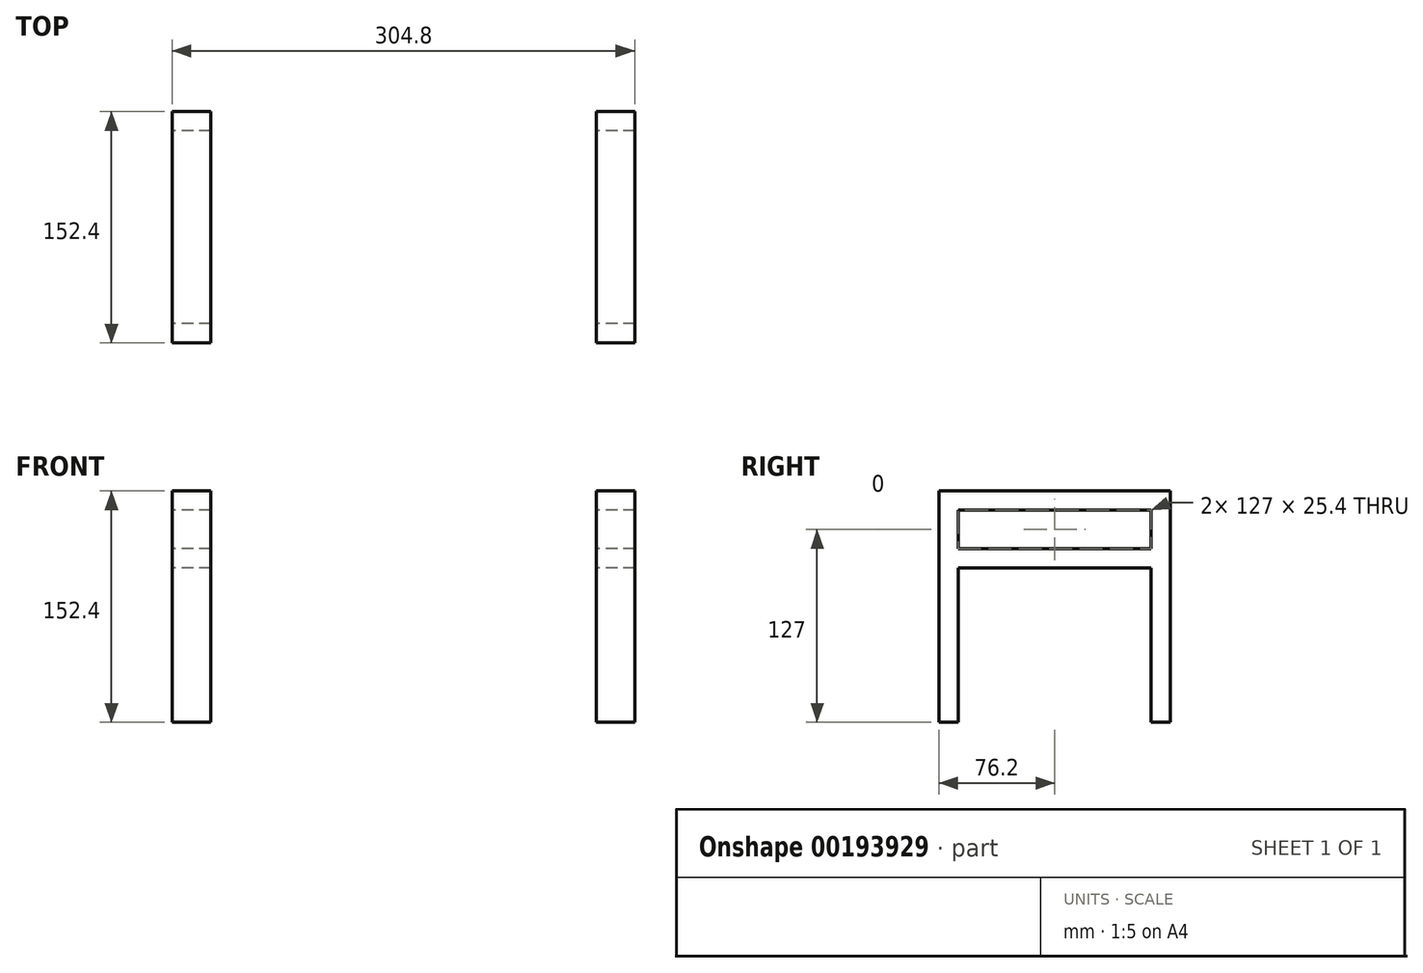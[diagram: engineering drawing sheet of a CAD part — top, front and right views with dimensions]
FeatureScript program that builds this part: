
annotation { "Feature Type Name" : "Feature", "Feature Type Description" : "" }
export const myFeature = defineFeature(function(context is Context, id is Id, definition is map)
    precondition{}
    {
        {
            var Q0;
            Q0=qCreatedBy(makeId("Front.planeOp"),FACE);
            var sketch = newSketch(context, id + "F0", { "sketchPlane" : qUnion([Q0])});
            skLineSegment(sketch, "E0.bottom", {"start": v(-150.3, 73.22) * mm, "end": v(154.5, 73.22) * mm});
            skLineSegment(sketch, "E0.top", {"start": v(-150.3, -79.18) * mm, "end": v(154.5, -79.18) * mm});
            skLineSegment(sketch, "E0.left", {"start": v(-150.3, 73.22) * mm, "end": v(-150.3, -79.18) * mm});
            skLineSegment(sketch, "E0.right", {"start": v(154.5, 73.22) * mm, "end": v(154.5, -79.18) * mm});
            skSolve(sketch);
        }
        {
            var Q0;
            Q0 = qSketchRegion(id + "F0", true);
            extrude(context, id + "F1", {"entities" : qUnion([Q0]), "depth" : 152.4 * mm});
        }
        {
            var Q0;
            Q0=makeQuery(id+"F1.opExtrude","SWEPT_FACE",FACE,{"disambiguationData":[OSD([sQuery(id+"F0.wireOp",EDGE,"E0.left")])]});
            var sketch = newSketch(context, id + "F2", { "sketchPlane" : qUnion([Q0])});
            skLineSegment(sketch, "E1.0", {"start": v(152.4, 60.52) * mm, "end": v(0, 60.52) * mm});
            skLineSegment(sketch, "E2.0", {"start": v(12.7, 73.22) * mm, "end": v(12.7, -79.18) * mm});
            skLineSegment(sketch, "E3.0", {"start": v(139.7, 73.22) * mm, "end": v(139.7, -79.18) * mm});
            skLineSegment(sketch, "E4.0", {"start": v(152.4, 35.12) * mm, "end": v(0, 35.12) * mm});
            skLineSegment(sketch, "E5.0", {"start": v(152.4, 22.42) * mm, "end": v(0, 22.42) * mm});
            skSolve(sketch);
        }
        {
            var Q0;
            {var subQ0=sQuery(id+"F2.wireOp",EDGE,"E3.0");var subQ1=sQuery(id+"F2.wireOp",EDGE,"E1.0");var subQ2=makeQuery(id+"F2.imprint","INTERSECT",VERTEX,{"derivedFrom":[subQ1,subQ0]});Q0=makeQuery(id+"F2.imprint","IMPRINT",FACE,{"disambiguationData":[TD([[makeQuery(id+"F2.imprint","IMPRINT",EDGE,{"disambiguationData":[TD([[subQ2,-1.0]])],"derivedFrom":subQ1}),1.0]])]});}
            var Q1;
            {var subQ0=sQuery(id+"F2.wireOp",EDGE,"E2.0");var subQ3=sQuery(id+"F2.wireOp",EDGE,"E5.0");var subQ4=makeQuery(id+"F2.imprint","INTERSECT",VERTEX,{"derivedFrom":[subQ0,subQ3]});Q1=makeQuery(id+"F2.imprint","IMPRINT",FACE,{"disambiguationData":[TD([[makeQuery(id+"F2.imprint","IMPRINT",EDGE,{"disambiguationData":[TD([[subQ4,1.0]])],"derivedFrom":subQ3}),1.0]])]});}
            extrude(context, id + "F3", {"entities" : qUnion([Q0, Q1]), "operationType" : NewBodyOperationType.REMOVE, "oppositeDirection" : true, "depth" : 304.8 * mm});
        }
        {
            var Q0;
            Q0=makeQuery(id+"F1.opExtrude","SWEPT_FACE",FACE,{"disambiguationData":[OSD([sQuery(id+"F0.wireOp",EDGE,"E0.bottom")])]});
            var sketch = newSketch(context, id + "F4", { "sketchPlane" : qUnion([Q0])});
            skLineSegment(sketch, "E6.0", {"start": v(-124.9, -152.4) * mm, "end": v(-124.9, 0) * mm});
            skLineSegment(sketch, "E7.0", {"start": v(129.1, -152.4) * mm, "end": v(129.1, 0) * mm});
            skSolve(sketch);
        }
        {
            var Q0;
            {var subQ0=sQuery(id+"F4.wireOp",EDGE,"E6.0");Q0=makeQuery(id+"F4.imprint","IMPRINT",FACE,{"disambiguationData":[TD([[makeQuery(id+"F4.imprint","IMPRINT",EDGE,{"derivedFrom":subQ0}),-1.0]])]});}
            extrude(context, id + "F5", {"entities" : qUnion([Q0]), "operationType" : NewBodyOperationType.REMOVE, "oppositeDirection" : true, "depth" : 152.4 * mm});
        }
    });
